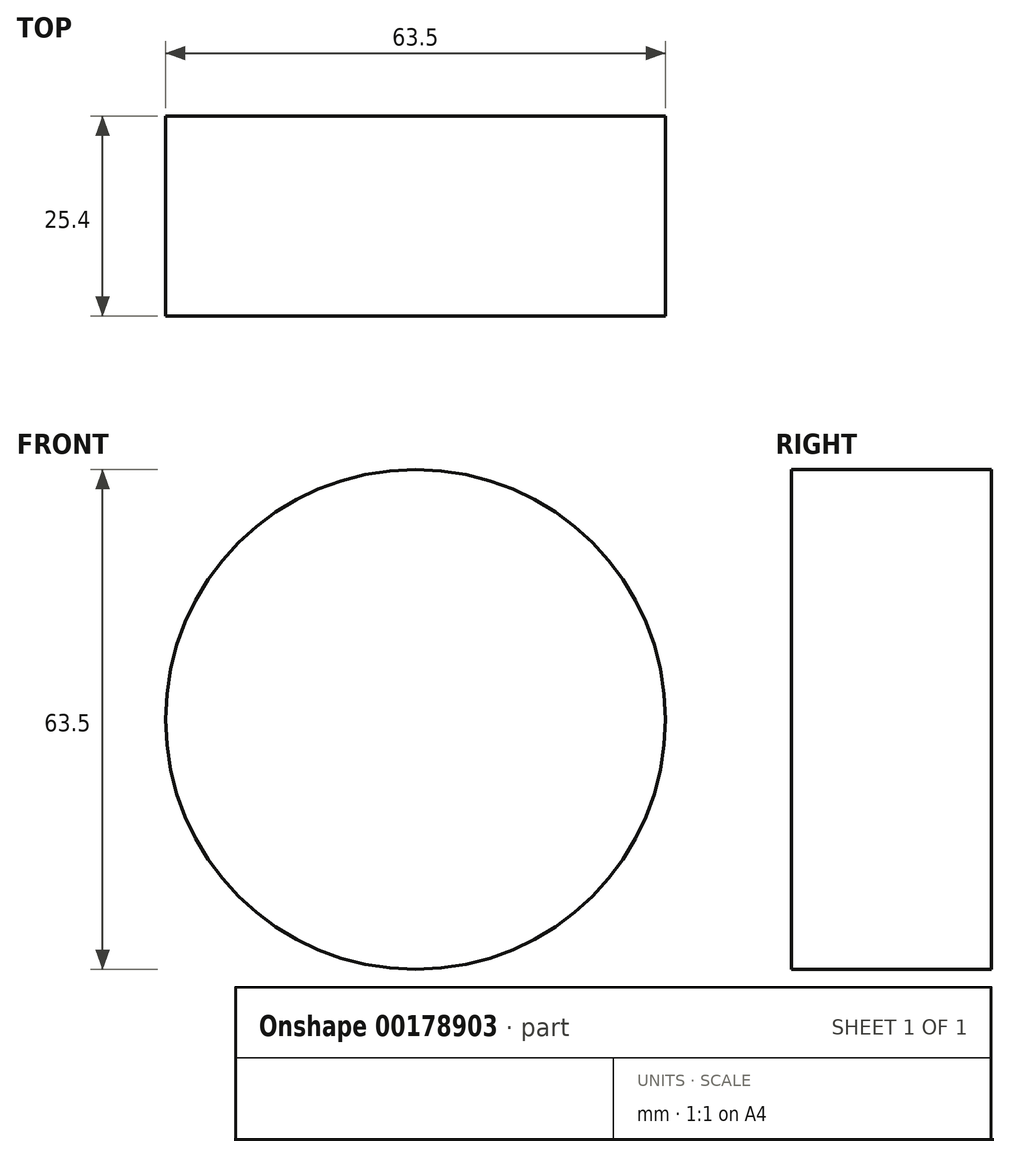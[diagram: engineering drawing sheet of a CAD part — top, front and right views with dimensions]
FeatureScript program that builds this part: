
annotation { "Feature Type Name" : "Feature", "Feature Type Description" : "" }
export const myFeature = defineFeature(function(context is Context, id is Id, definition is map)
    precondition{}
    {
        {
            var Q0;
            Q0=qCreatedBy(makeId("Front.planeOp"),FACE);
            var sketch = newSketch(context, id + "F0", { "sketchPlane" : qUnion([Q0])});
            skCircle(sketch, "E0", {"center": v(0, 0) * mm, "radius": 31.75 * mm});
            skSolve(sketch);
        }
        {
            var Q0;
            Q0 = qSketchRegion(id + "F0", true);
            extrude(context, id + "F1", {"entities" : qUnion([Q0]), "depth" : 25.4 * mm});
        }
    });
